# Revit family: PRD_FrankeWS_JntrlUnits_SiriusCleanerSink_SIRX832
name_source: partatom
category: Plumbing Fixtures
revit_build: Autodesk Revit 2018 (Build: 20190510_1515(x64)
units: mm (PartAtom-declared; Revit-internal decimal feet)

## family parameters
Always vertical = Yes
Cut with Voids When Loaded = No
OmniClass Number = 23.45.05.14
OmniClass Title = Plumbing Fixtures - Sanitary Washing Units
Part Type = Normal
Room Calculation Point = No
Round Connector Dimension = Use Diameter
Shared = No
Work Plane-Based = No

## types (1)
- SIRX832
    AssetType = Fixed
    BIMObjectName = PRD_AR_JanitorialUnits_SiriusCleanerSink_SIRX832
    Category = Pr_40_20_96_44, Janitorial sinks
    Color = Stainless steel
    Description = Cleaner sink wash basin combination, free standing or for wall mounting, stainless steel, surface satin finished, material thickness 1.2 mm, seamless welded bowl with diameter 360 x 272 x 135 mm, without overflow, 1 1/4" flat perforated waste, inclusive tap hole top right, sink with diameter 420 x 350 x 180 mm and revolving channel, 1 1/2" domed waste, drainage centric, inclusive stainless steel folding grid with rubber bumps, removable inspection cover, feet height adjustable.
    DrainSize = 1 1/2"
    DurationUnit = year
    Features = stainless steel, 1.20 mm, satin finished, wall mounting, 500x880x570 mm (WxHxD)
    Finish = Satin finished
    FinishAndMaterial = Stainless steel
    Form = Cleaner sink wash basin combination
    GrossWeight = 18.72 kg
    IfcExportAs = IfcSanitaryTerminalType
    IfcExportType = SINK
    LegsMaterial = PRD_AR_SyntheticBlack
    Manufacturer = KWC Group AG
    ManufacturerName = KWC Group AG
    ManufacturerURL = www.kwc.com
    Material = Stainless steel
    Model = SIRX832
    ModelNumber = 2000071907
    ModelReference = SIRX832
    NBSDescription = Janitorial units
    NBSReference = 45-35-70/401
    Name = SIRIUS Cleaner sink SIRX832
    NetWeight = 18.20 kg
    NominalDepth = 880 mm  [stored 2.88714 ft]
    NominalHeight = 880 mm  [stored 2.88714 ft]
    NominalLength = 570 mm  [stored 1.87008 ft]
    NominalWidth = 500 mm  [stored 1.64042 ft]
    ProductInformation = https://pim.kwc.com
    SinkMounting = Pedestal
    SinkType = Other
    Size = 500 x 880 x 570 mm
    Stainless Steel = PRD_AR_StainlessSteel_SatinFinished
    URL = www.kwc.com
    Uniclass2015Code = Pr_40_20_96_44
    Uniclass2015Title = Janitorial sinks
    Uniclass2015Version = Products v1.7
    Version = 1
    WarrantyDurationUnit = year
    WasteSize = 1 1/2"
    WasteSize Top = 1 1/4"
    WaterSupplyOverflowAndWasteHolesOverflow = No
    WaterSupplyOverflowAndWasteHolesWaste = Center-Back
    WaterSupplyOverflowAndWasteHolesWaterSupply = 32 mm  [stored 0.104987 ft]

note: [stored X ft] marks values corroborated as IEEE doubles in the binary element streams (Revit-internal decimal feet)

## geometry (parser evidence)
native form markers: Sweep x2
no freeform markers — native parametric forms only
